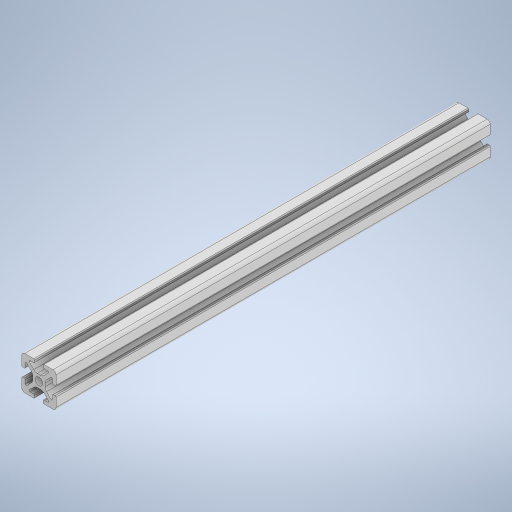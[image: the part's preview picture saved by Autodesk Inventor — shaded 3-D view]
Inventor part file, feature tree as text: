
AUTODESK INVENTOR PART (.ipt)
format: ipt  version: 2023 (Build 270158000, 158)  size: 418,304 bytes
history: mixed  units: in
note: dims shown in document units (in); Inventor stores cm internally (conversion verified against a paired STEP export)
features: extrude x1, sketch x1, projected_geometry x1, mirror x1, imported_body x1
ambient origin geometry x8: Origin, YZ Plane, XZ Plane, XY Plane, X Axis, Y Axis, Z Axis, Center Point
bodies: Solid1 (imported_parasolid)
feature tree (5):
  extrude  "Extrusion1"  [1 undecoded]
  sketch  "Sketch1"  dims[d0=2.0in d1=0.0in]
  projected_geometry  "Projected Loop1"
  mirror  "Mirror2"
  imported_body  NMx_Import_Brep_tag  [imported B-rep: ~75 faces, bbox_mm=[20.0, 20.0, 254.0]]
note: 1 required parameter value undecoded (feature->parameter linkage not recoverable at this tier; creation-order binding heuristic only, values carry confidence <= 0.55)
